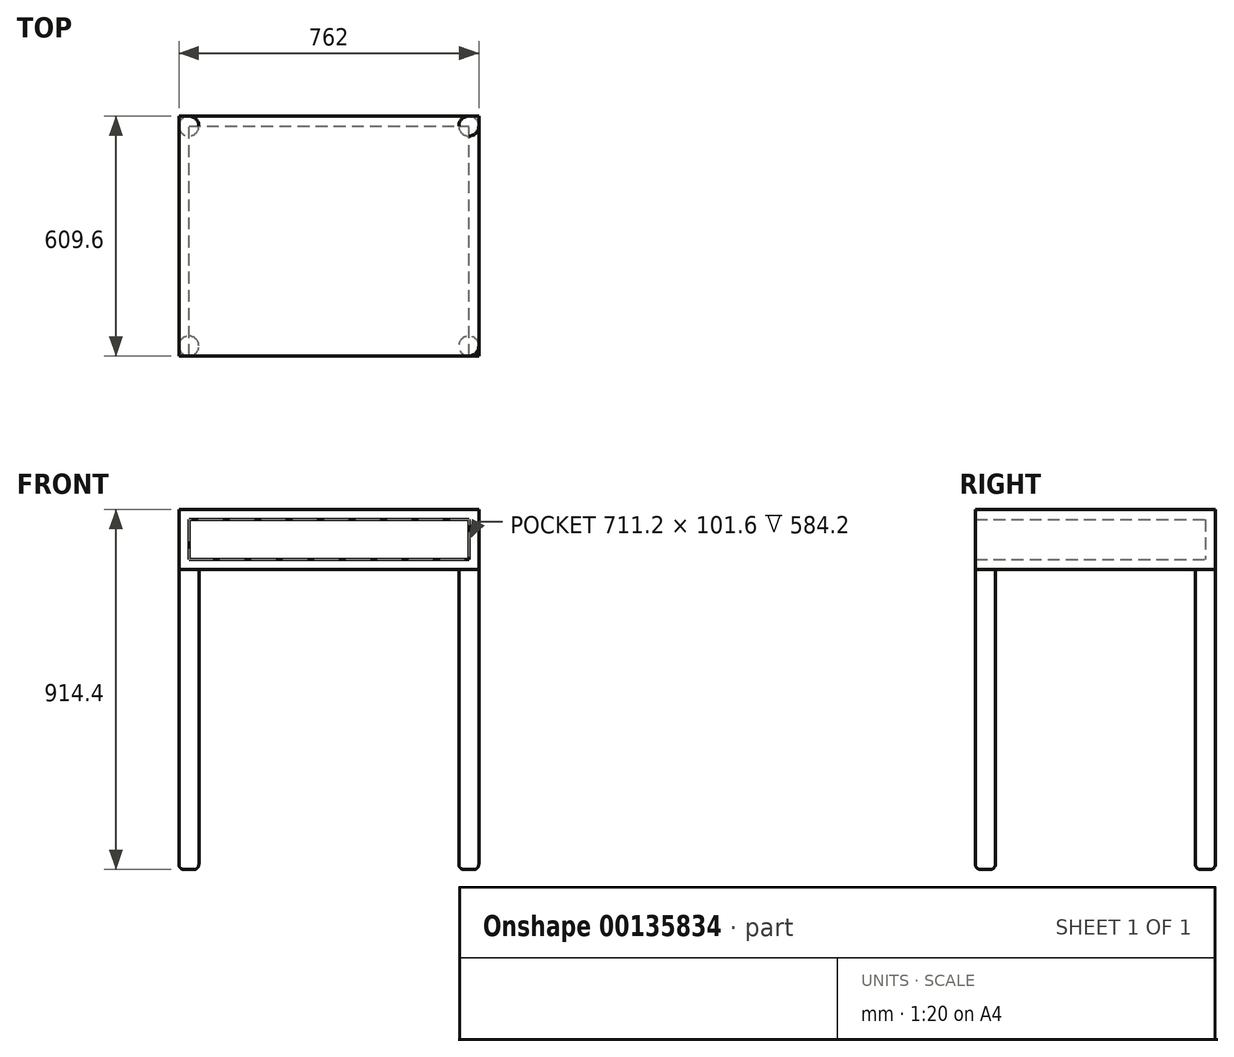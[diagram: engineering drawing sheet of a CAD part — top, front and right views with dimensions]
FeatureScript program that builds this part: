
annotation { "Feature Type Name" : "Feature", "Feature Type Description" : "" }
export const myFeature = defineFeature(function(context is Context, id is Id, definition is map)
    precondition{}
    {
        {
            var Q0;
            Q0=qCreatedBy(makeId("Front.planeOp"),FACE);
            var sketch = newSketch(context, id + "F0", { "sketchPlane" : qUnion([Q0])});
            skLineSegment(sketch, "E0.bottom", {"start": v(-381, 533.4) * mm, "end": v(381, 533.4) * mm});
            skLineSegment(sketch, "E0.top", {"start": v(-381, 381) * mm, "end": v(381, 381) * mm});
            skLineSegment(sketch, "E0.left", {"start": v(-381, 533.4) * mm, "end": v(-381, 381) * mm});
            skLineSegment(sketch, "E0.right", {"start": v(381, 533.4) * mm, "end": v(381, 381) * mm});
            skLineSegment(sketch, "E1", {"start": v(0, 381) * mm, "end": v(0, 0) * mm, "construction": true});
            skSolve(sketch);
        }
        {
            var Q0;
            Q0=makeQuery(id+"F0.imprint","IMPRINT",FACE,{"disambiguationData":[TD([[makeQuery(id+"F0.imprint","IMPRINT",EDGE,{"derivedFrom":sQuery(id+"F0.wireOp",EDGE,"E0.bottom")}),-1.0]])]});
            extrude(context, id + "F1", {"entities" : qUnion([Q0]), "endBound" : BoundingType.SYMMETRIC, "depth" : 609.6 * mm});
        }
        {
            var Q0;
            Q0=makeQuery(id+"F1.opExtrude","CAP_FACE",FACE,{"disambiguationData":[OSD([sQuery(id+"F0.wireOp",EDGE,"E0.bottom"),sQuery(id+"F0.wireOp",EDGE,"E0.top"),sQuery(id+"F0.wireOp",EDGE,"E0.left"),sQuery(id+"F0.wireOp",EDGE,"E0.right")])],"isStart":false});
            shell(context, id + "F2", {"entities" : qUnion([Q0]), "thickness" : 25.4 * mm});
        }
        {
            var Q0;
            Q0=qCreatedBy(makeId("Top.planeOp"),FACE);
            var sketch = newSketch(context, id + "F3", { "sketchPlane" : qUnion([Q0])});
            skCircle(sketch, "E2", {"center": v(-355.6, -279.4) * mm, "radius": 25.4 * mm});
            skCircle(sketch, "E3", {"center": v(355.6, -279.4) * mm, "radius": 25.4 * mm});
            skCircle(sketch, "E4", {"center": v(-355.6, 279.4) * mm, "radius": 25.4 * mm});
            skCircle(sketch, "E5", {"center": v(355.6, 279.4) * mm, "radius": 25.4 * mm});
            skSolve(sketch);
        }
        {
            var Q0;
            Q0=makeQuery(id+"F3.imprint","IMPRINT",FACE,{"disambiguationData":[TD([[makeQuery(id+"F3.imprint","IMPRINT",EDGE,{"derivedFrom":sQuery(id+"F3.wireOp",EDGE,"E4")}),1.0]])]});
            var Q1;
            Q1=makeQuery(id+"F3.imprint","IMPRINT",FACE,{"disambiguationData":[TD([[makeQuery(id+"F3.imprint","IMPRINT",EDGE,{"derivedFrom":sQuery(id+"F3.wireOp",EDGE,"E5")}),1.0]])]});
            var Q2;
            Q2=makeQuery(id+"F3.imprint","IMPRINT",FACE,{"disambiguationData":[TD([[makeQuery(id+"F3.imprint","IMPRINT",EDGE,{"derivedFrom":sQuery(id+"F3.wireOp",EDGE,"E3")}),1.0]])]});
            var Q3;
            Q3=makeQuery(id+"F3.imprint","IMPRINT",FACE,{"disambiguationData":[TD([[makeQuery(id+"F3.imprint","IMPRINT",EDGE,{"derivedFrom":sQuery(id+"F3.wireOp",EDGE,"E2")}),1.0]])]});
            extrude(context, id + "F4", {"entities" : qUnion([Q0, Q1, Q2, Q3]), "operationType" : NewBodyOperationType.ADD, "endBound" : BoundingType.SYMMETRIC, "depth" : 762 * mm});
        }
        {
            var Q0;
            Q0=makeQuery(id+"F4.opExtrude","CAP_EDGE",EDGE,{"disambiguationData":[OSD([sQuery(id+"F3.wireOp",EDGE,"E4")])],"isStart":true});
            var Q1;
            Q1=makeQuery(id+"F4.opExtrude","CAP_EDGE",EDGE,{"disambiguationData":[OSD([sQuery(id+"F3.wireOp",EDGE,"E2")])],"isStart":true});
            var Q2;
            Q2=makeQuery(id+"F4.opExtrude","CAP_EDGE",EDGE,{"disambiguationData":[OSD([sQuery(id+"F3.wireOp",EDGE,"E3")])],"isStart":true});
            var Q3;
            Q3=makeQuery(id+"F4.opExtrude","CAP_EDGE",EDGE,{"disambiguationData":[OSD([sQuery(id+"F3.wireOp",EDGE,"E5")])],"isStart":true});
            fillet(context, id + "F5", {"entities" : qUnion([Q0, Q1, Q2, Q3]), "radius" : 12.7 * mm, "tangentPropagation" : true, "allowEdgeOverflow" : false});
        }
    });
